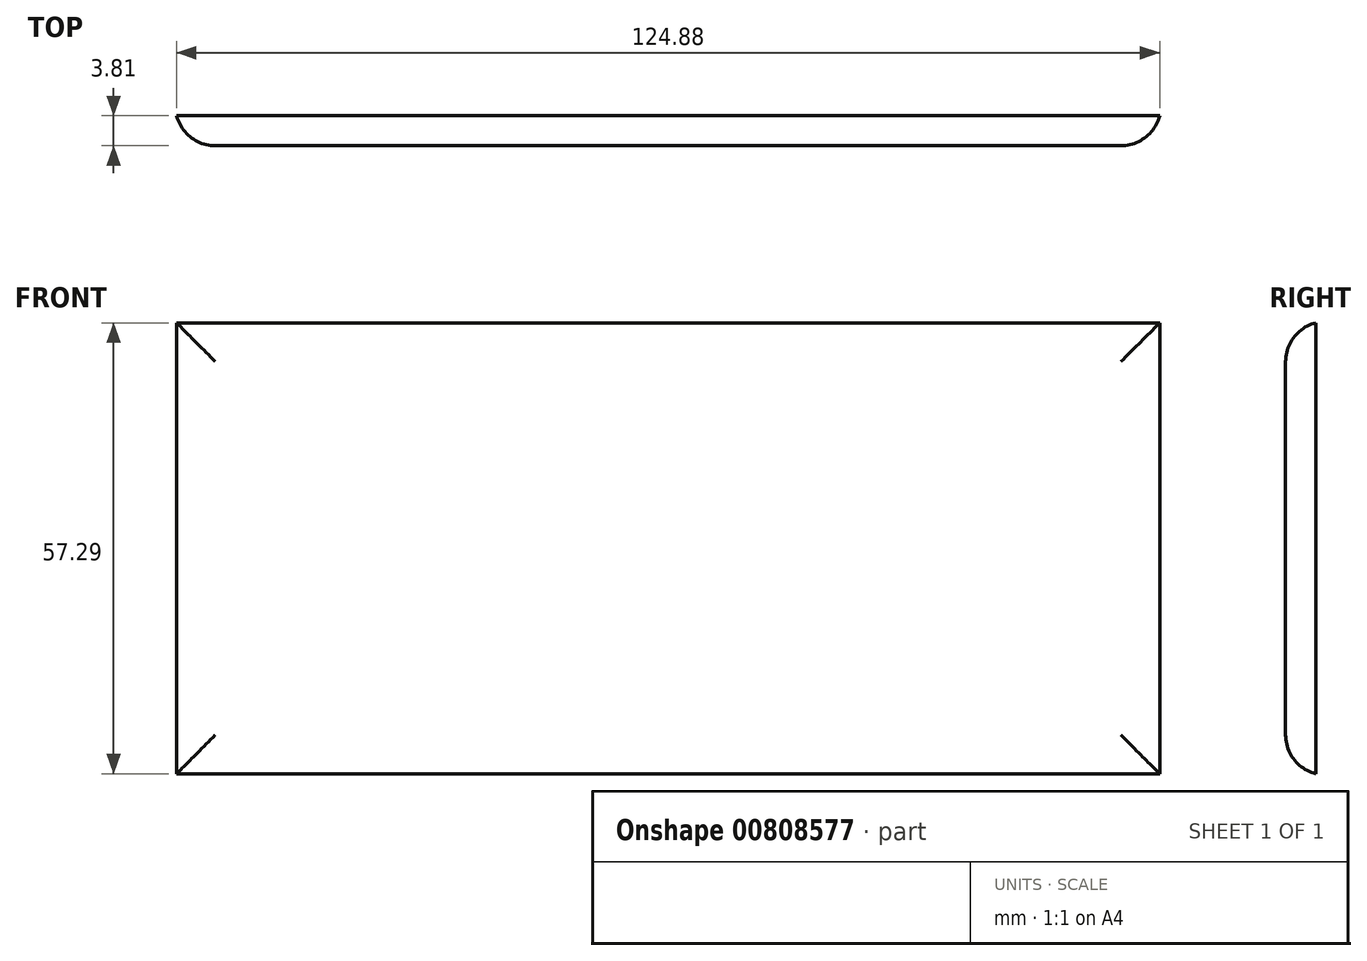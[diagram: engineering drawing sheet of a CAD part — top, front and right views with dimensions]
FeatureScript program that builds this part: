
annotation { "Feature Type Name" : "Feature", "Feature Type Description" : "" }
export const myFeature = defineFeature(function(context is Context, id is Id, definition is map)
    precondition{}
    {
        {
            var Q0;
            Q0=qCreatedBy(makeId("Front.planeOp"),FACE);
            var sketch = newSketch(context, id + "F0", { "sketchPlane" : qUnion([Q0])});
            skLineSegment(sketch, "E0.bottom", {"start": v(-59.48, 28.55) * mm, "end": v(65.4, 28.55) * mm});
            skLineSegment(sketch, "E0.top", {"start": v(-59.48, -28.74) * mm, "end": v(65.4, -28.74) * mm});
            skLineSegment(sketch, "E0.left", {"start": v(-59.48, 28.55) * mm, "end": v(-59.48, -28.74) * mm});
            skLineSegment(sketch, "E0.right", {"start": v(65.4, 28.55) * mm, "end": v(65.4, -28.74) * mm});
            skSolve(sketch);
        }
        {
            var Q0;
            Q0=makeQuery(id+"F0.imprint","IMPRINT",FACE,{"disambiguationData":[TD([[makeQuery(id+"F0.imprint","IMPRINT",EDGE,{"derivedFrom":sQuery(id+"F0.wireOp",EDGE,"E0.bottom")}),-1.0]])]});
            extrude(context, id + "F1", {"entities" : qUnion([Q0]), "depth" : 3.8 * mm, "offsetDistance" : 25.4 * mm});
        }
        {
            var Q0;
            Q0=makeQuery(id+"F1.opExtrude","CAP_EDGE",EDGE,{"disambiguationData":[OSD([sQuery(id+"F0.wireOp",EDGE,"E0.bottom")])],"isStart":false});
            var Q1;
            Q1=makeQuery(id+"F1.opExtrude","CAP_EDGE",EDGE,{"disambiguationData":[OSD([sQuery(id+"F0.wireOp",EDGE,"E0.left")])],"isStart":false});
            var Q2;
            Q2=makeQuery(id+"F1.opExtrude","CAP_EDGE",EDGE,{"disambiguationData":[OSD([sQuery(id+"F0.wireOp",EDGE,"E0.right")])],"isStart":false});
            var Q3;
            Q3=makeQuery(id+"F1.opExtrude","CAP_EDGE",EDGE,{"disambiguationData":[OSD([sQuery(id+"F0.wireOp",EDGE,"E0.top")])],"isStart":false});
            fillet(context, id + "F2", {"entities" : qUnion([Q0, Q1, Q2, Q3]), "radius" : 5.08 * mm, "tangentPropagation" : true, "allowEdgeOverflow" : false});
        }
    });
